# Revit family: CMB-WM350F-AA
name_source: partatom
category: 機械設備
revit_build: Autodesk Revit 2016 (Build: 20150220_1215(x64)
units: mm (PartAtom-declared; Revit-internal decimal feet)

## family parameters
OmniClass タイトル = Climate Control (HVAC)
OmniClass 番号 = 23.75.00.00
パーツ タイプ = 標準
ロード時にボイドで切り取り = いいえ
丸型コネクタ寸法 = 半径を使用
作業面に基づく = いいえ
共有 = いいえ
常に垂直 = はい
部屋の計算ポイント = いいえ

## types (1)
- CMB-WM350F-AA
    Connectable Outdoor/Heat source Unit Capacity = PURY-M200~350YNW-A1(-BS)/PURY-EM200~350YNW-A1(-BS)
    Connection pipe of outdoor/heat source unit to M200(High press. Pipe)(O.D.) = 15.88  [stored 0.0520997 ft]
    Connection pipe of outdoor/heat source unit to M200(Low press. Pipe)(O.D.) = 19.05  [stored 0.0625 ft]
    Connection pipe of outdoor/heat source unit to M250/M300(High press. Pipe)(O.D.) = 15.88  [stored 0.0520997 ft]
    Connection pipe of outdoor/heat source unit to M250/M300(Low press. Pipe)(O.D.) = 22.2  [stored 0.0728346 ft]
    Connection pipe of outdoor/heat source unit to M350(High press. Pipe)(O.D.) = 15.88  [stored 0.0520997 ft]
    Connection pipe of outdoor/heat source unit to M350(Low press. Pipe)(O.D.) = 28.58  [stored 0.0937664 ft]
    Cooling Current (A) = 6.52
    Cooling Power Input (kW) = 1.5
    Depth = 500  [stored 1.64042 ft]
    Drain pipe_radius = 13.35  [stored 0.0437992 ft]
    Equip_No. = 0
    External Finish = Galvanized steel plate
    Field pipe size[W/WP/WL101-150](Max 20m/40m/60m)(I.D.) = 32.6/32.6/32.6
    Field pipe size[W/WP/WL10](Max 20m/40m/60m)(I.D.) = 12/12/12
    Field pipe size[W/WP/WL11-15](Max 20m/40m/60m)(I.D.) = 12/12/15.5
    Field pipe size[W/WP/WL151-250](Max 20m/40m/60m)(I.D.) = 32.6/32.6/39.6
    Field pipe size[W/WP/WL16-25](Max 20m/40m/60m)(I.D.) = 15.5/15.5/15.5
    Field pipe size[W/WP/WL251-300](Max 20m/40m/60m)(I.D.) = 32.6/39.6/50.8
    Field pipe size[W/WP/WL26-32](Max 20m/40m/60m)(I.D.) = 15.5/19.9/19.9
    Field pipe size[W/WP/WL301-750](Max 20m/40m/60m)(I.D.) = 50.8/50.8/50.8
    Field pipe size[W/WP/WL33-50](Max 20m/40m/60m)(I.D.) = 19.9/19.9/19.9
    Field pipe size[W/WP/WL51-63](Max 20m/40m/60m)(I.D.) = 19.9/25.2/25.2
    Field pipe size[W/WP/WL64-80](Max 20m/40m/60m)(I.D.) = 25.2/25.2/25.2
    Field pipe size[W/WP/WL81-100](Max 20m/40m/60m)(I.D.) = 25.2/25.2/32.6
    Heating Current (A) = 6.52
    Heating Power Input (kW) = 1.5
    Height = 1500  [stored 4.92126 ft]
    Hertz = 50 Hz
    Indoor unit capacity connectable to 1 branch = Model WP/W/WL80 or smaller (Use optional joint pipe combining 2 branches when the total unit capacity exceeds WP/W/WL80.)
    Number of branch = 6
    Phase = 1
    SerialNumber = 0
    Sound Pressure Level (dB(A)) = 54
    Space View = はい
    Subcategory = HVAC
    TagNumber = 0
    URL = http://www.mitsubishielectric.com
    Unit Weight (kg) = 196
    Voltage = 230 V
    Water piping diameter To Indoor unit(O.D.) = 22  [stored 0.0721785 ft]
    Water piping diameter To Sub HBC(O.D.) = 42  [stored 0.137795 ft]
    Width = 800  [stored 2.62467 ft]
    モデル = CMB-WM350F-AA
    製造元 = Mitsubishi Electric Corporation
    説明 = HBC

note: [stored X ft] marks values corroborated as IEEE doubles in the binary element streams (Revit-internal decimal feet)

## geometry (parser evidence)
native form markers: Blend x40, Sweep x2
no freeform markers — native parametric forms only
